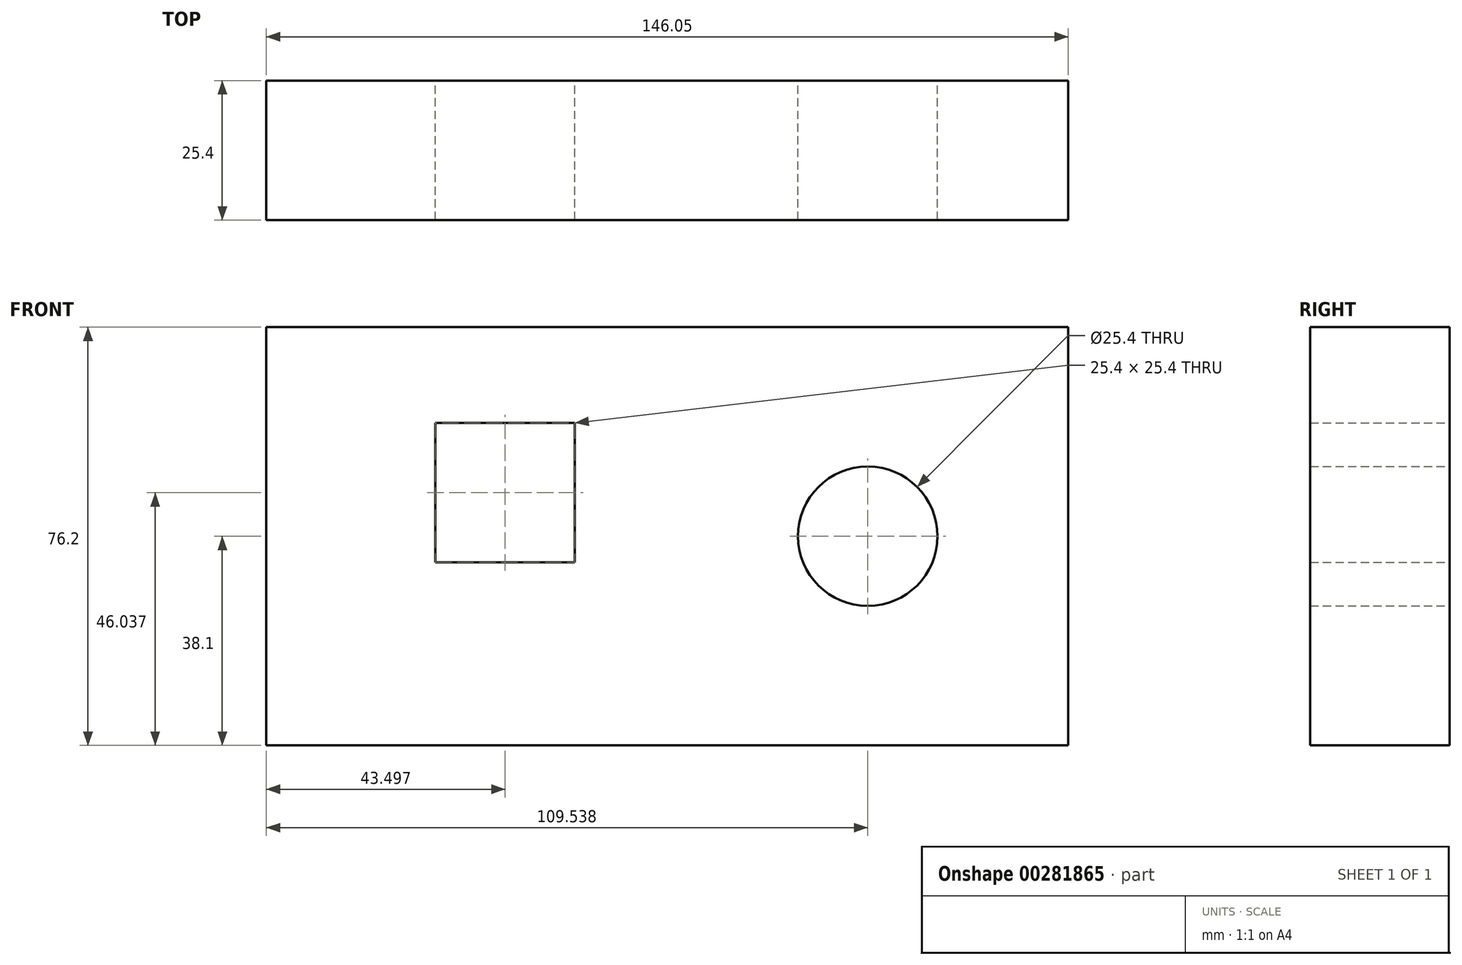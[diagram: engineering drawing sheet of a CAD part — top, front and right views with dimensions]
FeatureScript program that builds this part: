
annotation { "Feature Type Name" : "Feature", "Feature Type Description" : "" }
export const myFeature = defineFeature(function(context is Context, id is Id, definition is map)
    precondition{}
    {
        {
            var Q0;
            Q0=qCreatedBy(makeId("Front.planeOp"),FACE);
            var sketch = newSketch(context, id + "F0", { "sketchPlane" : qUnion([Q0])});
            skLineSegment(sketch, "E0.bottom", {"start": v(0, 0) * mm, "end": v(-146.05, 0) * mm});
            skLineSegment(sketch, "E0.top", {"start": v(0, 76.2) * mm, "end": v(-146.05, 76.2) * mm});
            skLineSegment(sketch, "E0.left", {"start": v(0, 0) * mm, "end": v(0, 76.2) * mm});
            skLineSegment(sketch, "E0.right", {"start": v(-146.05, 0) * mm, "end": v(-146.05, 76.2) * mm});
            skLineSegment(sketch, "E1.bottom", {"start": v(-115.25, 33.34) * mm, "end": v(-89.85, 33.34) * mm});
            skLineSegment(sketch, "E1.top", {"start": v(-115.25, 58.74) * mm, "end": v(-89.85, 58.74) * mm});
            skLineSegment(sketch, "E1.left", {"start": v(-115.25, 33.34) * mm, "end": v(-115.25, 58.74) * mm});
            skLineSegment(sketch, "E1.right", {"start": v(-89.85, 33.34) * mm, "end": v(-89.85, 58.74) * mm});
            skCircle(sketch, "E2", {"center": v(-36.51, 38.1) * mm, "radius": 12.7 * mm});
            skSolve(sketch);
        }
        {
            var Q0;
            Q0=makeQuery(id+"F0.imprint","IMPRINT",FACE,{"disambiguationData":[TD([[makeQuery(id+"F0.imprint","IMPRINT",EDGE,{"derivedFrom":sQuery(id+"F0.wireOp",EDGE,"E0.bottom")}),-1.0]])]});
            extrude(context, id + "F1", {"entities" : qUnion([Q0]), "depth" : 25.4 * mm});
        }
    });
